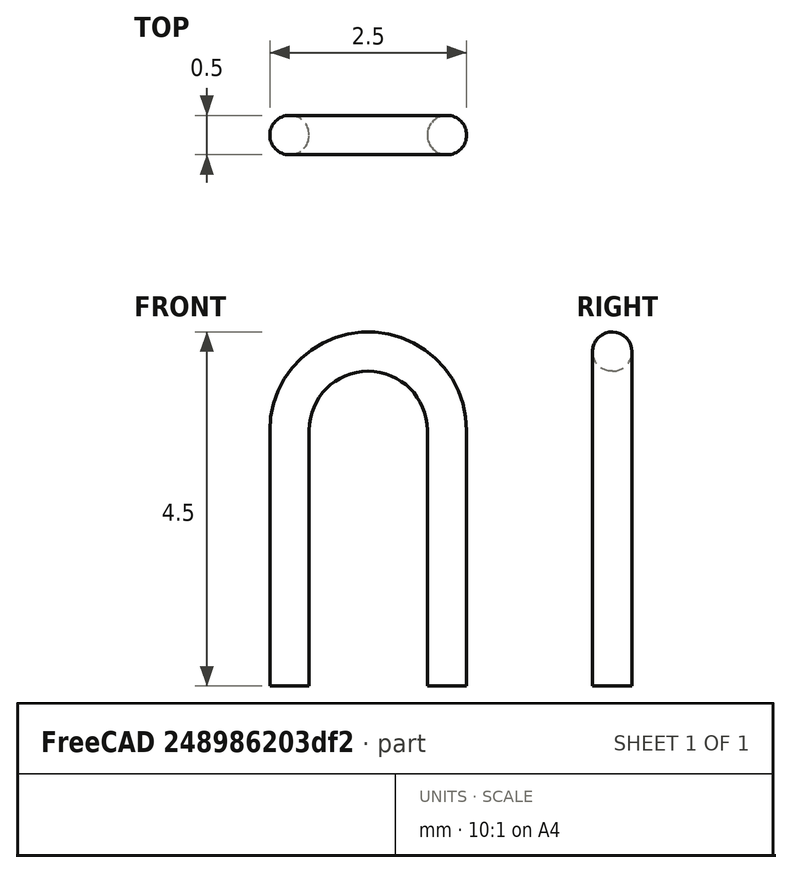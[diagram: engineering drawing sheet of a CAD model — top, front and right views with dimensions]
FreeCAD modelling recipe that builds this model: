
FCSTD DOCUMENT  (FreeCAD 0.17R12018 (Git))
Label: Test_Point_Bridge_Pitch2.0mm_Drill0.7mm
License: All rights reserved
LicenseURL: http://en.wikipedia.org/wiki/All_rights_reserved
objects: Sketcher::SketchObject×2, Spreadsheet::Sheet×1, PartDesign::SubtractivePipe×1, PartDesign::Body×1
note: 5 computed .brp shape members not serialized (recipe doc carries the construction recipe); baked Part::Feature solids carry a one-line shape summary decoded from their .brp

FEATURE [Sketcher::SketchObject] Sketch
  MapMode = 5
  Placement = pos=(0,0,-3) rot=(0,0,1;0rad)
  Support = -> [XY_Plane]
  superPlacement = pos=(0,0,-3) rot=(0,0,1;0rad)
  expr: Constraints[1] = dims.DWire / 2
  sketch-geometry (1):
    g0: Circle CenterX=0 CenterY=0 CenterZ=0 NormalX=0 NormalY=0 NormalZ=1 Radius=0.25
  constraints (2):
    c: Coincident(g0,g-1)
    c: Radius(g0) = 0.25
FEATURE [Spreadsheet::Sheet] Spreadsheet  label="dims"
  cells = A1="DWire"; B1(DWire)=0.5; A2="Pitch"; B2(Pitch)=2
FEATURE [Sketcher::SketchObject] Sketch001
  MapMode = 5
  Placement = pos=(0,0,0) rot=(1,0,0;1.5708rad)
  Support = -> [XZ_Plane]
  expr: Constraints[10] = dims.DWire / 2
  expr: Constraints[3] = dims.Pitch
  sketch-geometry (4):
    g0: LineSegment StartX=0 StartY=-3 StartZ=0 EndX=0 EndY=0.25 EndZ=0
    g1: LineSegment StartX=2 StartY=0.25 StartZ=0 EndX=2 EndY=-3 EndZ=0
    g2: LineSegment [constr] StartX=0 StartY=0.25 StartZ=0 EndX=2 EndY=0.25 EndZ=0
    g3: ArcOfCircle CenterX=1 CenterY=0.25 CenterZ=0 NormalX=0 NormalY=0 NormalZ=1 Radius=1 StartAngle=0 EndAngle=3.14159
  constraints (13):
    c: PointOnObject(g0,g-2)
    c: Vertical(g0)
    c: Vertical(g1)
    c: DistanceX(g0,g1) = 2
    c: Coincident(g2,g0)
    c: Coincident(g2,g1)
    c: Horizontal(g2)
    c: PointOnObject(g3,g2)
    c: Coincident(g3,g0)
    c: Coincident(g3,g1)
    c: DistanceY(g-1,g3) = 0.25
    c: DistanceY(g0,g-1) = 3
    c: Equal(g1,g0)
FEATURE [PartDesign::SubtractivePipe] SubtractivePipe
  AuxilleryCurvelinear = true
  AuxillerySpineTangent = false
  Binormal = (0,0,0)
  Mode = 0
  Profile = -> Sketch
  Spine = -> Sketch001
  SpineTangent = false
  Transformation = 0
  Transition = 0
FEATURE [PartDesign::Body] Body  label="Test_Point_Bridge_Pitch2.0mm_Drill0.7mm"
  Group = -> [Sketch,Sketch001,SubtractivePipe]
  Origin = -> Origin
  Tip = -> SubtractivePipe
